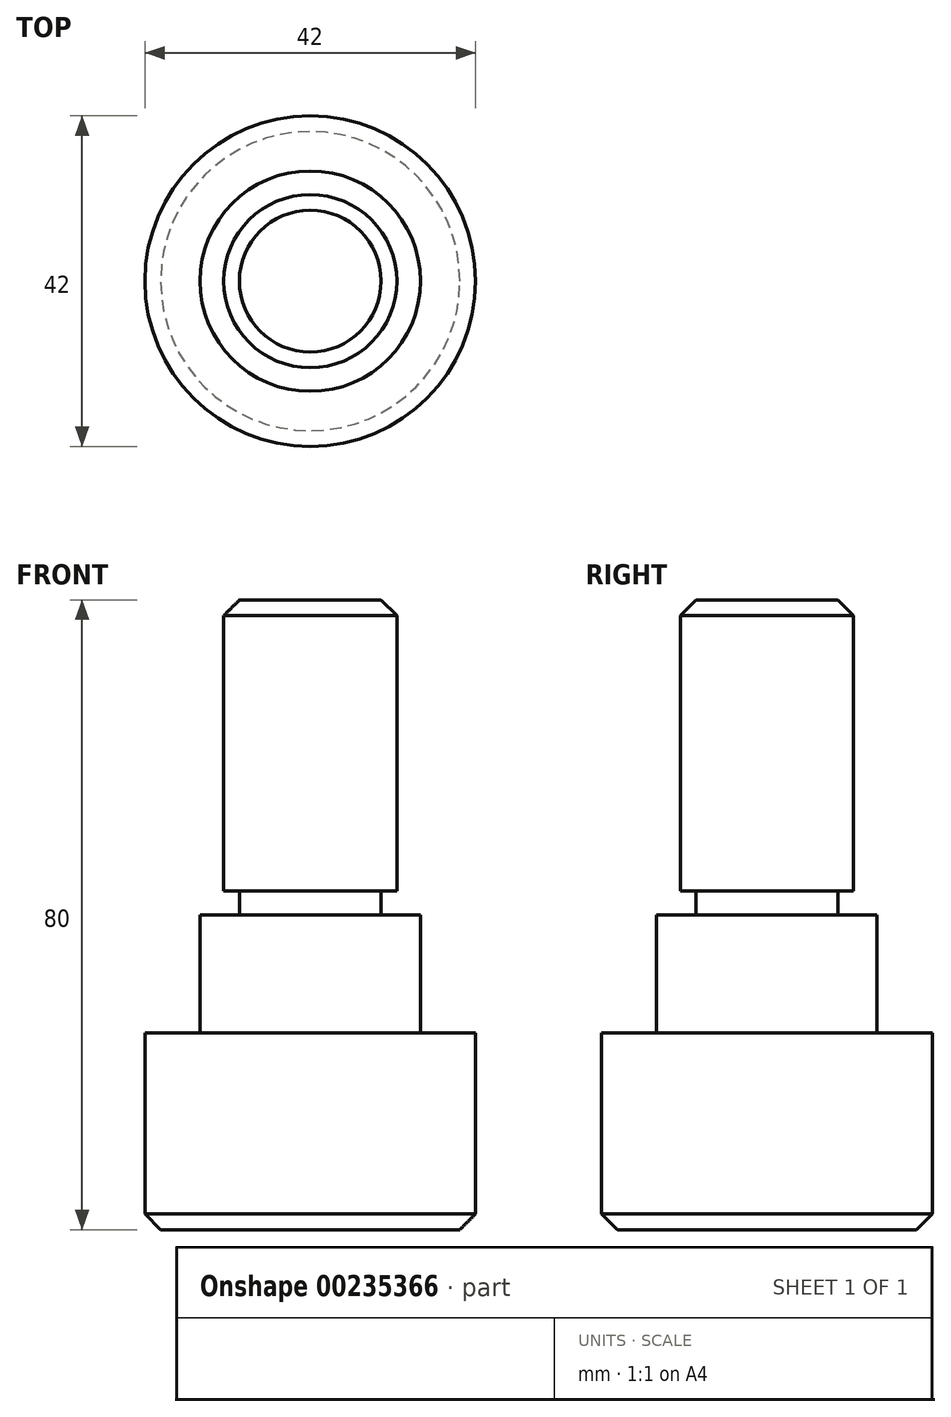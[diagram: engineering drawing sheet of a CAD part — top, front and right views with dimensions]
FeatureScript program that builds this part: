
annotation { "Feature Type Name" : "Feature", "Feature Type Description" : "" }
export const myFeature = defineFeature(function(context is Context, id is Id, definition is map)
    precondition{}
    {
        {
            var Q0;
            Q0=qCreatedBy(makeId("Front.planeOp"),FACE);
            var sketch = newSketch(context, id + "F0", { "sketchPlane" : qUnion([Q0])});
            skLineSegment(sketch, "E0", {"start": v(0, 0) * mm, "end": v(21, 0) * mm});
            skLineSegment(sketch, "E1", {"start": v(21, 0) * mm, "end": v(21, 25) * mm});
            skLineSegment(sketch, "E2", {"start": v(21, 25) * mm, "end": v(14, 25) * mm});
            skLineSegment(sketch, "E3", {"start": v(9, 40) * mm, "end": v(9, 43) * mm});
            skLineSegment(sketch, "E4", {"start": v(9, 43) * mm, "end": v(11, 43) * mm});
            skLineSegment(sketch, "E5", {"start": v(11, 43) * mm, "end": v(11, 80) * mm});
            skLineSegment(sketch, "E6", {"start": v(11, 80) * mm, "end": v(0, 80) * mm});
            skLineSegment(sketch, "E7", {"start": v(0, 80) * mm, "end": v(0, 0) * mm});
            skLineSegment(sketch, "E8", {"start": v(14, 40) * mm, "end": v(14, 25) * mm});
            skPoint(sketch, "E9.orphan", {"position": v(11, 25) * mm});
            skLineSegment(sketch, "E10", {"start": v(9, 40) * mm, "end": v(14, 40) * mm});
            skSolve(sketch);
        }
        {
            var Q0;
            Q0=makeQuery(id+"F0.imprint","IMPRINT",FACE,{"disambiguationData":[TD([[makeQuery(id+"F0.imprint","IMPRINT",EDGE,{"derivedFrom":sQuery(id+"F0.wireOp",EDGE,"E0")}),1.0]])]});
            var Q1;
            Q1=sQuery(id+"F0.wireOp",EDGE,"E7");
            revolve(context, id + "F1", {"entities" : qUnion([Q0]), "axis" : qUnion([Q1]), "revolveType" : RevolveType.FULL});
        }
        {
            var Q0;
            Q0=makeQuery(id+"F1.opRevolve","SWEPT_EDGE",EDGE,{"disambiguationData":[OSD([sQuery(id+"F0.wireOp",EDGE,"E5"),sQuery(id+"F0.wireOp",EDGE,"E6")])]});
            var Q1;
            Q1=makeQuery(id+"F1.opRevolve","SWEPT_EDGE",EDGE,{"disambiguationData":[OSD([sQuery(id+"F0.wireOp",EDGE,"E0"),sQuery(id+"F0.wireOp",EDGE,"E1")])]});
            chamfer(context, id + "F2", {"entities" : qUnion([Q0, Q1]), "chamferType" : ChamferType.OFFSET_ANGLE, "width" : 2 * mm, "oppositeDirection" : false, "angle" : 45 * degree, "tangentPropagation" : true});
        }
    });
